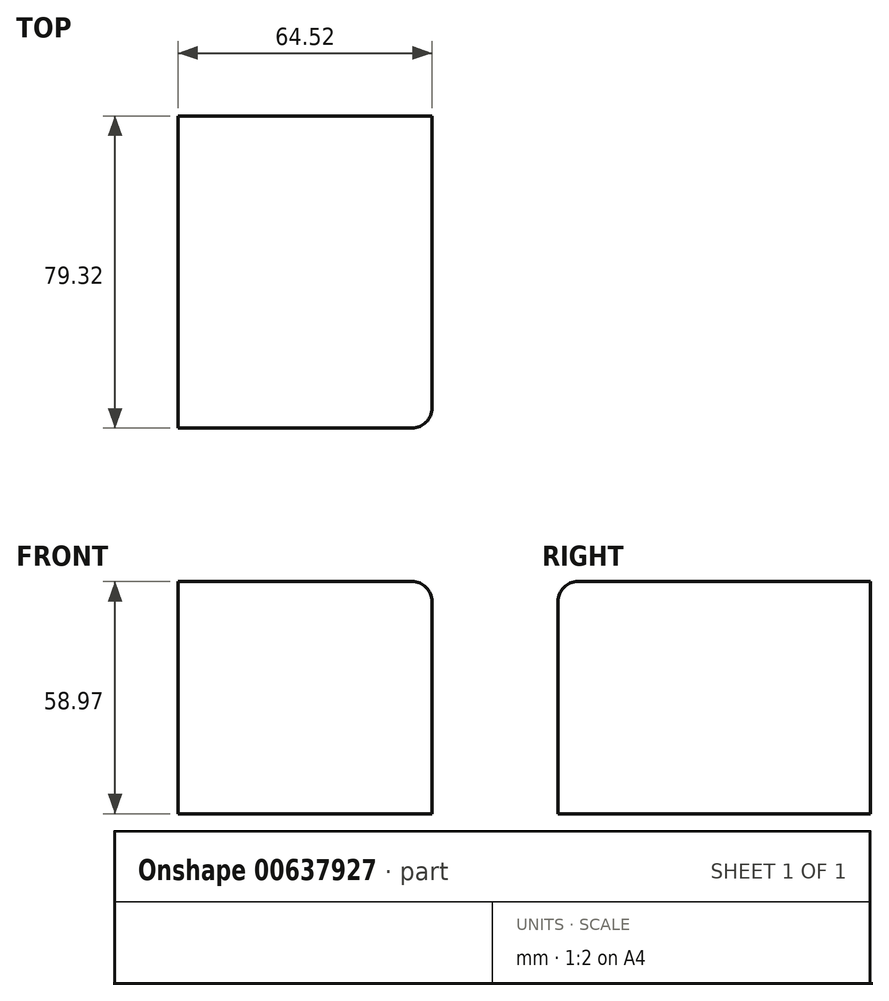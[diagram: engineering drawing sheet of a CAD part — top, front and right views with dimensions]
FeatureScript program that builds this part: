
annotation { "Feature Type Name" : "Feature", "Feature Type Description" : "" }
export const myFeature = defineFeature(function(context is Context, id is Id, definition is map)
    precondition{}
    {
        {
            var Q0;
            Q0=qCreatedBy(makeId("Front.planeOp"),FACE);
            var sketch = newSketch(context, id + "F0", { "sketchPlane" : qUnion([Q0])});
            skLineSegment(sketch, "E0.bottom", {"start": v(31.63, 0) * mm, "end": v(-32.9, 0) * mm});
            skLineSegment(sketch, "E0.top", {"start": v(31.63, 58.97) * mm, "end": v(-32.9, 58.97) * mm});
            skLineSegment(sketch, "E0.left", {"start": v(31.63, 0) * mm, "end": v(31.63, 58.97) * mm});
            skLineSegment(sketch, "E0.right", {"start": v(-32.9, 0) * mm, "end": v(-32.9, 58.97) * mm});
            skPoint(sketch, "E0.middle", {"position": v(-0.63, 29.48) * mm});
            skSolve(sketch);
        }
        {
            var Q0;
            Q0=makeQuery(id+"F0.imprint","IMPRINT",FACE,{"disambiguationData":[TD([[makeQuery(id+"F0.imprint","IMPRINT",EDGE,{"derivedFrom":sQuery(id+"F0.wireOp",EDGE,"E0.bottom")}),-1.0]])]});
            extrude(context, id + "F1", {"entities" : qUnion([Q0]), "depth" : 79.32 * mm, "offsetDistance" : 25.4 * mm});
        }
        {
            var Q0;
            Q0=makeQuery(id+"F1.opExtrude","CAP_EDGE",EDGE,{"disambiguationData":[OSD([sQuery(id+"F0.wireOp",EDGE,"E0.top")])],"isStart":false});
            var Q1;
            Q1=makeQuery(id+"F1.opExtrude","SWEPT_EDGE",EDGE,{"disambiguationData":[OSD([sQuery(id+"F0.wireOp",EDGE,"E0.top"),sQuery(id+"F0.wireOp",EDGE,"E0.left")])]});
            var Q2;
            Q2=makeQuery(id+"F1.opExtrude","CAP_EDGE",EDGE,{"disambiguationData":[OSD([sQuery(id+"F0.wireOp",EDGE,"E0.left")])],"isStart":false});
            fillet(context, id + "F2", {"entities" : qUnion([Q0, Q1, Q2]), "radius" : 5.08 * mm, "tangentPropagation" : true, "allowEdgeOverflow" : false});
        }
    });
